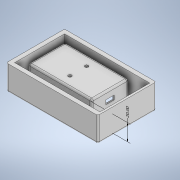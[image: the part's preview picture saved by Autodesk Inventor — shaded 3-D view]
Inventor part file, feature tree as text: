
AUTODESK INVENTOR PART (.ipt)
format: ipt  version: 2020 (Build 240168000, 168)  size: 231,936 bytes
history: native  units: mm
features: extrude x7, sketch x6, projected_geometry x4, fillet x3, other x2, hole x1
ambient origin geometry x8: Origin, YZ Plane, XZ Plane, XY Plane, X Axis, Y Axis, Z Axis, Center Point
bodies: Solid1 (feature_tree)
feature tree (23):
  other  "Annotations"
  sketch  "Sketch1"  dims[d0=100.0mm d1=60.0mm]
  extrude  "Extrusion1"  Depth=60.0mm
  extrude  "Extrusion2"  TaperAngle=180.0deg  [1 undecoded]
  extrude  "Extrusion3"  Depth=73.0mm
  extrude  "Extrusion4"  Depth=110.0mm
  extrude  "Extrusion5"  Depth=76.0mm
  fillet  "Fillet1"  Radius=44.0mm
  hole  "Hole1"  [1 undecoded]
  extrude  "Extrusion6"  Depth=2.5mm TaperAngle=0.0deg
  fillet  "Fillet2"  Radius=2.5mm
  extrude  "Extrusion7"  Depth=10.0mm
  fillet  "Fillet3"  Radius=5.0mm
  sketch  "Sketch2"  dims[d2=5.0mm d3=180.0deg]
  sketch  "Sketch4"  dims[d4=5.0mm d5=73.0mm]
  projected_geometry  "Projected Loop3"
  projected_geometry  "Projected Loop4"
  projected_geometry  "Projected Loop5"
  sketch  "Sketch5"  dims[d6=40.0mm d7=110.0mm]
  sketch  "Sketch6"  dims[d8=70.0mm d9=76.0mm d10=44.0mm]
  sketch  "Sketch7"  dims[d11=30.0mm d12=0.0mm d13=22.0mm d14=0.0mm d15=2.5mm d16=0.0mm d17=2.5mm d18=0.0mm d19=10.0mm d20=5.0mm d21=10.0mm d22=0.0mm d23=2.0mm d24=10.0mm d25=10.0mm d26=1.5mm d27=6.0mm d28=2.5mm d29=1.0mm d30=14.3117mm d31=40.0mm d32=20.594885mm d33=4.0mm d34=4.0mm d35=1.5mm d36=0.0mm d37=2.0mm d46=2.5mm d47=27.5mm d48=0.0mm d55=2.0mm d52=7.759428mm d53=7.333746mm d54=20.0mm]
  projected_geometry  "Project Cut Edges5"
  other  "Linear Dimension 2"
note: 2 required parameter values undecoded (feature->parameter linkage not recoverable at this tier; creation-order binding heuristic only, values carry confidence <= 0.55)
